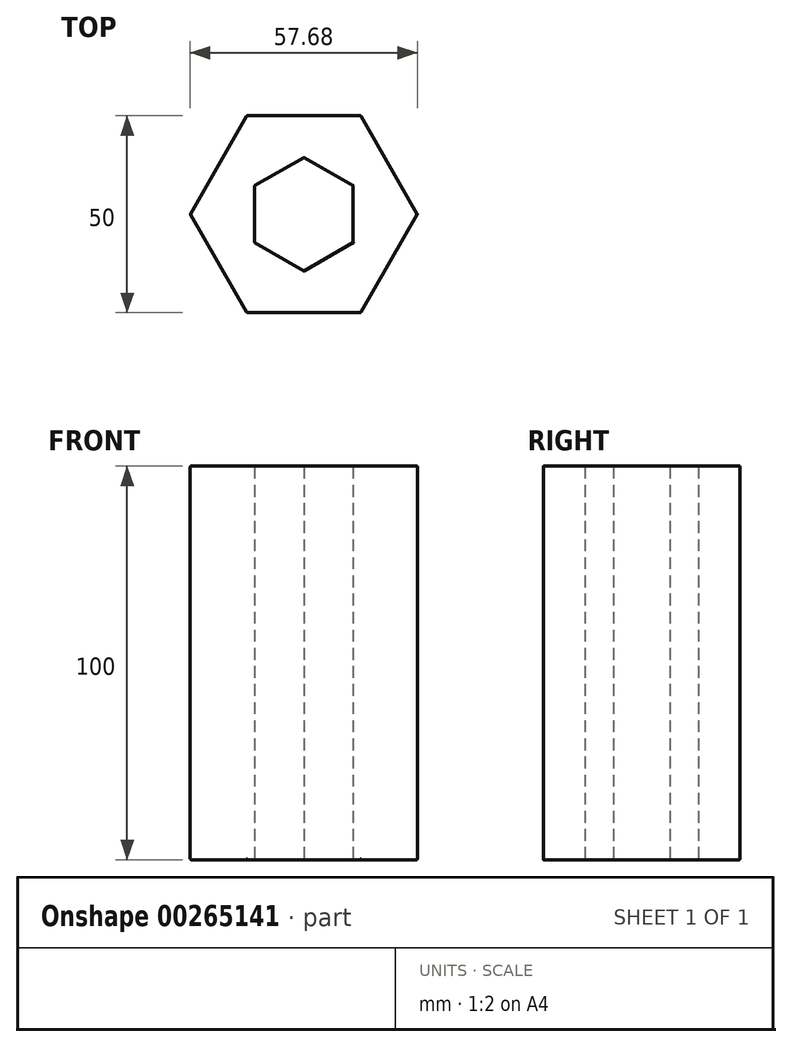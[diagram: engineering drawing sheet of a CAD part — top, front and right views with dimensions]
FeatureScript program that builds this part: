
annotation { "Feature Type Name" : "Feature", "Feature Type Description" : "" }
export const myFeature = defineFeature(function(context is Context, id is Id, definition is map)
    precondition{}
    {
        {
            var Q0;
            Q0=qCreatedBy(makeId("Top.planeOp"),FACE);
            var sketch = newSketch(context, id + "F0", { "sketchPlane" : qUnion([Q0])});
            skCircle(sketch, "E0.cCircle", {"center": v(0, 0) * mm, "radius": 25 * mm, "construction": true});
            skLineSegment(sketch, "E0.0", {"start": v(28.87, 0) * mm, "end": v(14.43, -25) * mm});
            skLineSegment(sketch, "E0.1", {"start": v(14.43, -25) * mm, "end": v(-14.43, -25) * mm});
            skLineSegment(sketch, "E0.2", {"start": v(-14.43, -25) * mm, "end": v(-28.87, 0) * mm});
            skLineSegment(sketch, "E0.3", {"start": v(-28.87, 0) * mm, "end": v(-14.43, 25) * mm});
            skLineSegment(sketch, "E0.4", {"start": v(-14.43, 25) * mm, "end": v(14.43, 25) * mm});
            skLineSegment(sketch, "E0.5", {"start": v(14.43, 25) * mm, "end": v(28.87, 0) * mm});
            skPoint(sketch, "E0.0.midPoint", {"position": v(21.65, -12.5) * mm});
            skCircle(sketch, "E1.cCircle", {"center": v(0, 0) * mm, "radius": 12.5 * mm, "construction": true});
            skLineSegment(sketch, "E1.0", {"start": v(0, 14.43) * mm, "end": v(12.5, 7.22) * mm});
            skLineSegment(sketch, "E1.1", {"start": v(12.5, 7.22) * mm, "end": v(12.5, -7.22) * mm});
            skLineSegment(sketch, "E1.2", {"start": v(12.5, -7.22) * mm, "end": v(0, -14.43) * mm});
            skLineSegment(sketch, "E1.3", {"start": v(0, -14.43) * mm, "end": v(-12.5, -7.22) * mm});
            skLineSegment(sketch, "E1.4", {"start": v(-12.5, -7.22) * mm, "end": v(-12.5, 7.22) * mm});
            skLineSegment(sketch, "E1.5", {"start": v(-12.5, 7.22) * mm, "end": v(0, 14.43) * mm});
            skPoint(sketch, "E1.0.midPoint", {"position": v(6.25, 10.83) * mm});
            skSolve(sketch);
        }
        {
            var Q0;
            Q0=makeQuery(id+"F0.imprint","IMPRINT",FACE,{"disambiguationData":[TD([[makeQuery(id+"F0.imprint","IMPRINT",EDGE,{"derivedFrom":sQuery(id+"F0.wireOp",EDGE,"E0.0")}),-1.0]])]});
            extrude(context, id + "F1", {"entities" : qUnion([Q0]), "depth" : 100 * mm});
        }
        {
            var Q0;
            Q0=makeQuery(id+"F1.opExtrude","CAP_FACE",FACE,{"disambiguationData":[OSD([sQuery(id+"F0.wireOp",EDGE,"E0.0"),sQuery(id+"F0.wireOp",EDGE,"E0.1"),sQuery(id+"F0.wireOp",EDGE,"E0.2"),sQuery(id+"F0.wireOp",EDGE,"E0.3"),sQuery(id+"F0.wireOp",EDGE,"E0.4"),sQuery(id+"F0.wireOp",EDGE,"E0.5"),sQuery(id+"F0.wireOp",EDGE,"E1.0"),sQuery(id+"F0.wireOp",EDGE,"E1.1"),sQuery(id+"F0.wireOp",EDGE,"E1.2"),sQuery(id+"F0.wireOp",EDGE,"E1.3"),sQuery(id+"F0.wireOp",EDGE,"E1.4"),sQuery(id+"F0.wireOp",EDGE,"E1.5")])],"isStart":false});
            var Q1;
            Q1=makeQuery(id+"F1.opExtrude","SWEPT_FACE",FACE,{"disambiguationData":[OSD([sQuery(id+"F0.wireOp",EDGE,"E0.0")])]});
            var Q2;
            Q2=makeQuery(id+"F1.opExtrude","SWEPT_FACE",FACE,{"disambiguationData":[OSD([sQuery(id+"F0.wireOp",EDGE,"E0.5")])]});
            var Q3;
            Q3=makeQuery(id+"F1.opExtrude","SWEPT_FACE",FACE,{"disambiguationData":[OSD([sQuery(id+"F0.wireOp",EDGE,"E0.4")])]});
            var Q4;
            Q4=makeQuery(id+"F1.opExtrude","SWEPT_FACE",FACE,{"disambiguationData":[OSD([sQuery(id+"F0.wireOp",EDGE,"E0.3")])]});
            var Q5;
            Q5=makeQuery(id+"F1.opExtrude","SWEPT_FACE",FACE,{"disambiguationData":[OSD([sQuery(id+"F0.wireOp",EDGE,"E0.2")])]});
            fillet(context, id + "F2", {"entities" : qUnion([Q0, Q1, Q2, Q3, Q4, Q5]), "radius" : 0.2 * mm, "tangentPropagation" : true, "allowEdgeOverflow" : false});
        }
    });
